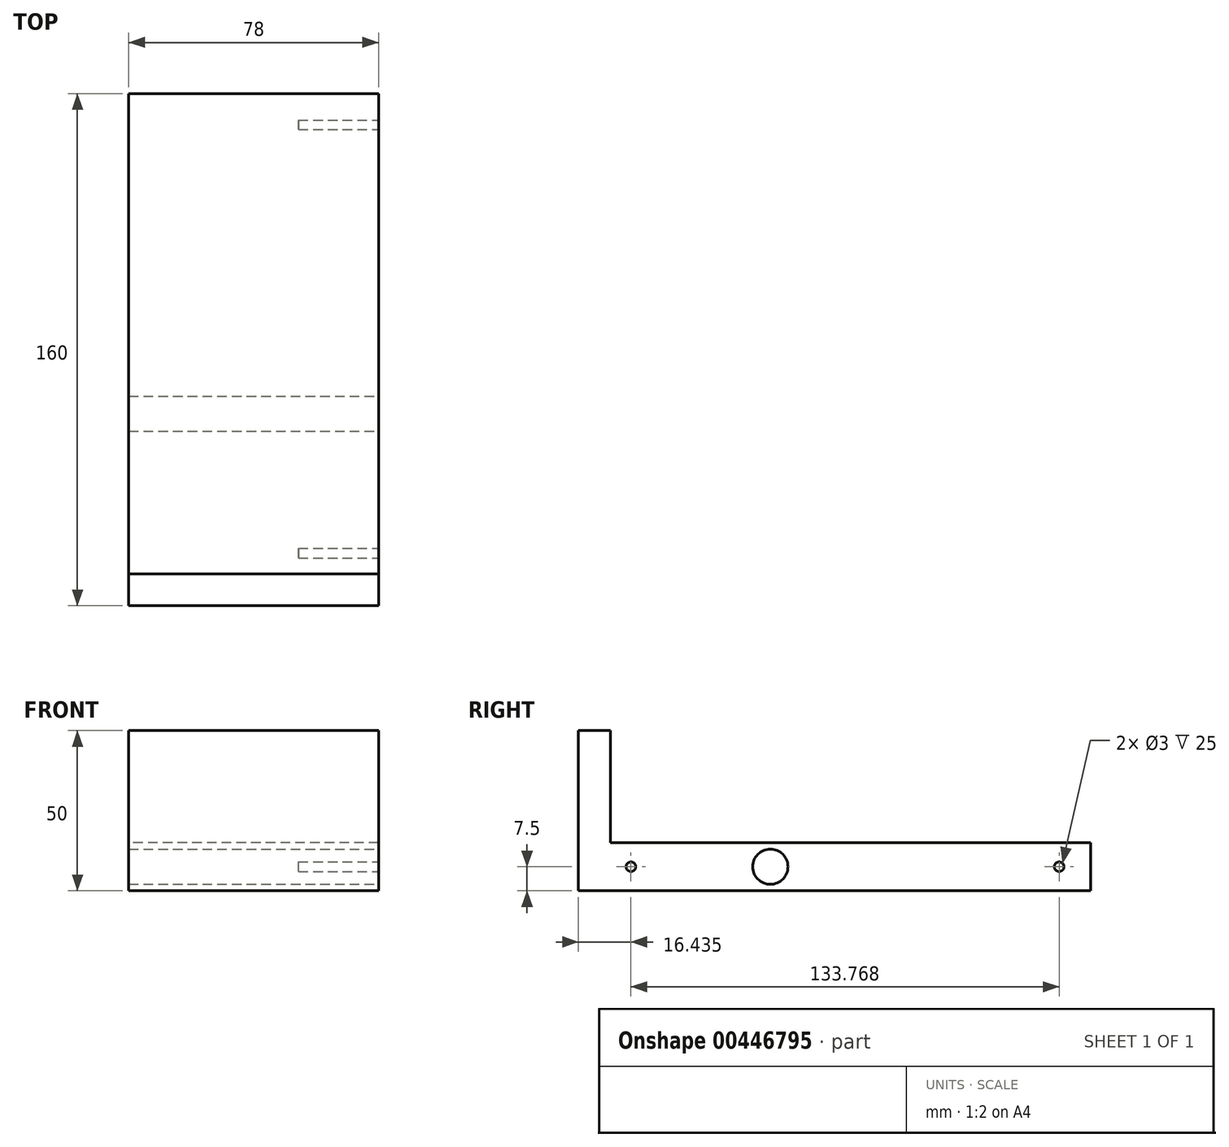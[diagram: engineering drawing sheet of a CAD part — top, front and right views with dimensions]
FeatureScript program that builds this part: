
annotation { "Feature Type Name" : "Feature", "Feature Type Description" : "" }
export const myFeature = defineFeature(function(context is Context, id is Id, definition is map)
    precondition{}
    {
        {
            var Q0;
            Q0=qCreatedBy(makeId("Right.planeOp"),FACE);
            var sketch = newSketch(context, id + "F0", { "sketchPlane" : qUnion([Q0])});
            skLineSegment(sketch, "E0", {"start": v(0, 0) * mm, "end": v(0, 50) * mm});
            skLineSegment(sketch, "E1", {"start": v(0, 50) * mm, "end": v(10, 50) * mm});
            skLineSegment(sketch, "E2", {"start": v(10, 50) * mm, "end": v(10, 15) * mm});
            skLineSegment(sketch, "E3", {"start": v(10, 15) * mm, "end": v(160, 15) * mm});
            skLineSegment(sketch, "E4", {"start": v(160, 15) * mm, "end": v(160, 0) * mm});
            skLineSegment(sketch, "E5", {"start": v(160, 0) * mm, "end": v(0, 0) * mm});
            skSolve(sketch);
        }
        {
            var Q0;
            Q0=qSketchRegion(id+"F0",true);
            extrude(context, id + "F1", {"entities" : qUnion([Q0]), "endBound" : BoundingType.SYMMETRIC, "depth" : 78 * mm});
        }
        {
            var Q0;
            Q0=makeQuery(id+"F1.opExtrude","CAP_FACE",FACE,{"disambiguationData":[OSD([sQuery(id+"F0.wireOp",EDGE,"E0"),sQuery(id+"F0.wireOp",EDGE,"E1"),sQuery(id+"F0.wireOp",EDGE,"E2"),sQuery(id+"F0.wireOp",EDGE,"E3"),sQuery(id+"F0.wireOp",EDGE,"E4"),sQuery(id+"F0.wireOp",EDGE,"E5")])],"isStart":false});
            var sketch = newSketch(context, id + "F2", { "sketchPlane" : qUnion([Q0])});
            skCircle(sketch, "E6", {"center": v(60, 7.5) * mm, "radius": 5.5 * mm});
            skLineSegment(sketch, "E7.0.0", {"start": v(0, 0) * mm, "end": v(160, 0) * mm});
            skLineSegment(sketch, "E7.0.1", {"start": v(160, 0) * mm, "end": v(160, 15) * mm});
            skLineSegment(sketch, "E7.0.2", {"start": v(160, 15) * mm, "end": v(10, 15) * mm});
            skLineSegment(sketch, "E7.0.3", {"start": v(10, 15) * mm, "end": v(10, 50) * mm});
            skLineSegment(sketch, "E7.0.4", {"start": v(10, 50) * mm, "end": v(0, 50) * mm});
            skLineSegment(sketch, "E7.0.5", {"start": v(0, 50) * mm, "end": v(0, 0) * mm});
            skSolve(sketch);
        }
        {
            var Q0;
            Q0=makeQuery(id+"F2.imprint","IMPRINT",FACE,{"disambiguationData":[TD([[makeQuery(id+"F2.imprint","IMPRINT",EDGE,{"derivedFrom":sQuery(id+"F2.wireOp",EDGE,"E6")}),1.0]])]});
            extrude(context, id + "F3", {"entities" : qUnion([Q0]), "operationType" : NewBodyOperationType.REMOVE, "oppositeDirection" : true, "depth" : 100 * mm});
        }
        {
            var Q0;
            Q0=makeQuery(id+"F1.opExtrude","CAP_FACE",FACE,{"disambiguationData":[OSD([sQuery(id+"F0.wireOp",EDGE,"E0"),sQuery(id+"F0.wireOp",EDGE,"E1"),sQuery(id+"F0.wireOp",EDGE,"E2"),sQuery(id+"F0.wireOp",EDGE,"E3"),sQuery(id+"F0.wireOp",EDGE,"E4"),sQuery(id+"F0.wireOp",EDGE,"E5")])],"isStart":false});
            var sketch = newSketch(context, id + "F4", { "sketchPlane" : qUnion([Q0])});
            skCircle(sketch, "E8", {"center": v(150.2, 7.5) * mm, "radius": 1.5 * mm});
            skPoint(sketch, "E8.centerSnap0", {"position": v(160, 7.5) * mm});
            skCircle(sketch, "E9", {"center": v(16.43, 7.5) * mm, "radius": 1.5 * mm});
            skSolve(sketch);
        }
        {
            var Q0;
            Q0=qSketchRegion(id+"F4",true);
            extrude(context, id + "F5", {"entities" : qUnion([Q0]), "operationType" : NewBodyOperationType.REMOVE, "oppositeDirection" : true, "depth" : 25 * mm});
        }
    });
